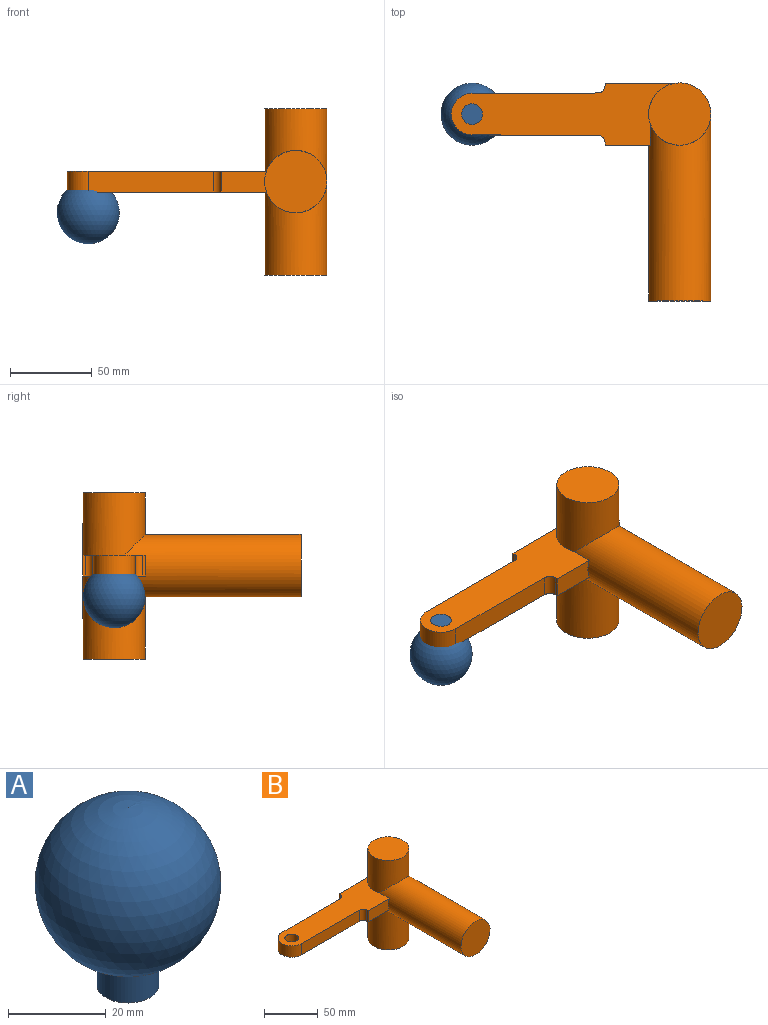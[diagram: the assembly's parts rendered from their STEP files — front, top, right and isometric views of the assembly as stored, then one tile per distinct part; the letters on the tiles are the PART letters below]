
ASSEMBLY  parts=2 mates=1
PART A: 3 faces, bbox 38.1x38.1x44.5 mm
  f0: cylinder r=6.35mm len=12.7mm, axis (0,0,1), area 296.8mm2, adj f1,f2
  f1: plane 12.7x12.7mm, normal (0,0,-1), area 126.7mm2, adj f0
  f2: sphere r=19.05mm, area 4430mm2, adj f0
PART B: 17 faces, bbox 158.8x133.4x101.6 mm
  f0: plane 45.72x12.7mm, normal (0,1,0), area 580.6mm2, adj f2,f3,f8,f9
  f1: plane 27.76x12.7mm, normal (0,-1,0), area 343.3mm2, adj f2,f4,f8,f10
  f2: plane 139.7x38.1mm, normal (0,0,1), area 3330.9mm2, adj f0,f1,f3,f4,f9,f10,f11,f12
  f3: cylinder r=19.05mm len=101.6mm, axis (0,0,-1), area 10288.6mm2, adj f0,f2,f4,f5,f6,f8
  f4: cylinder r=19.05mm len=114.3mm, axis (0,1,0), area 12024.3mm2, adj f1,f2,f3,f7,f8
  f5: plane 38.1x38.1mm, normal (0,0,1), area 1140.1mm2, adj f3
  f6: plane 38.1x38.1mm, normal (0,0,-1), area 1140.1mm2, adj f3
  f7: plane 38.1x38.1mm, normal (0,-1,0), area 1140.1mm2, adj f4
  f8: plane 139.7x38.1mm, normal (0,0,-1), area 3330.9mm2, adj f0,f1,f3,f4,f9,f10,f11,f12
  f9: plane 12.7x1.54mm, normal (-1,0,0), area 19.5mm2, adj f0,f2,f8,f16
  f10: plane 12.7x1.54mm, normal (-1,0,0), area 19.5mm2, adj f1,f2,f8,f15
  f11: plane 76.72x12.7mm, normal (0,1,0), area 974.4mm2, adj f2,f8,f13,f16
  f12: plane 76.72x12.7mm, normal (0,-1,0), area 974.4mm2, adj f2,f8,f13,f15
  f13: cylinder r=12.7mm len=25.4mm, axis (0,0,1), area 506.7mm2, adj f2,f8,f11,f12
  f14: cylinder r=6.35mm len=12.7mm, axis (0,0,1), area 506.7mm2, adj f2,f8
  f15: cylinder r=4.57mm len=12.7mm, axis (0,0,-1), area 91mm2, adj f2,f8,f10,f12
  f16: cylinder r=4.57mm len=12.7mm, axis (0,0,-1), area 91mm2, adj f2,f8,f9,f11
PLACE A rot(axis=(1,0,0),180deg) t=(-127,0,38.1)mm
PLACE B at identity
MATE fastened A.f0 <-> B.f14  axis (0,0,1) through (-127,0,63.5)mm
